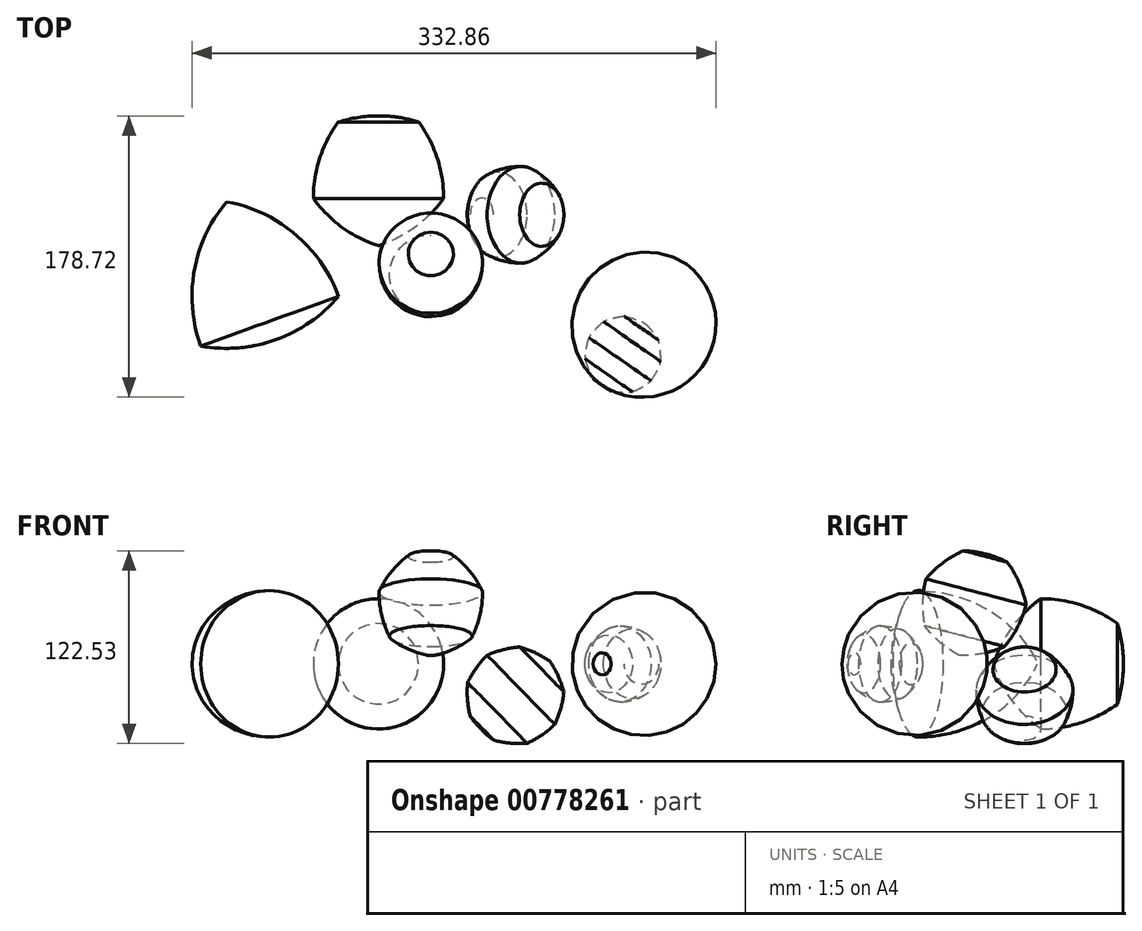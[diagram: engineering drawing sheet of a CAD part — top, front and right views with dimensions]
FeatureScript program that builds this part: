
annotation { "Feature Type Name" : "Feature", "Feature Type Description" : "" }
export const myFeature = defineFeature(function(context is Context, id is Id, definition is map)
    precondition{}
    {
        {
            var Q0;
            Q0=qCreatedBy(makeId("Top.planeOp"),FACE);
            var sketch = newSketch(context, id + "F0", { "sketchPlane" : qUnion([Q0])});
            skCircle(sketch, "E0.cCircle", {"center": v(-111.5, -42.3) * mm, "radius": 26.86 * mm, "construction": true});
            skLineSegment(sketch, "E0.0", {"start": v(-129.74, 8.22) * mm, "end": v(-58.63, -51.78) * mm});
            skLineSegment(sketch, "E0.1", {"start": v(-58.63, -51.78) * mm, "end": v(-146.14, -83.36) * mm});
            skLineSegment(sketch, "E0.2", {"start": v(-146.14, -83.36) * mm, "end": v(-129.74, 8.22) * mm});
            skPoint(sketch, "E0.0.midPoint", {"position": v(-94.18, -21.78) * mm});
            skCircle(sketch, "E1", {"center": v(-58.63, -51.78) * mm, "radius": 93.04 * mm});
            skCircle(sketch, "E2", {"center": v(-129.74, 8.22) * mm, "radius": 93.04 * mm});
            skCircle(sketch, "E3", {"center": v(-146.14, -83.36) * mm, "radius": 93.04 * mm});
            skLineSegment(sketch, "E4", {"start": v(-129.74, 8.22) * mm, "end": v(-98.18, -79.3) * mm});
            skSolve(sketch);
        }
        {
            var Q0;
            {var subQ0=sQuery(id+"F0.wireOp",EDGE,"E0.2");Q0=makeQuery(id+"F0.imprint","IMPRINT",FACE,{"disambiguationData":[TD([[makeQuery(id+"F0.imprint","IMPRINT",EDGE,{"derivedFrom":subQ0}),1.0]])]});}
            var Q1;
            {var subQ1=sQuery(id+"F0.wireOp",EDGE,"E0.2");Q1=makeQuery(id+"F0.imprint","IMPRINT",FACE,{"disambiguationData":[TD([[makeQuery(id+"F0.imprint","IMPRINT",EDGE,{"derivedFrom":subQ1}),-1.0]])]});}
            var Q2;
            {var subQ0=sQuery(id+"F0.wireOp",EDGE,"E2");var subQ3=sQuery(id+"F0.wireOp",EDGE,"E4");var subQ5=makeQuery(id+"F0.imprint","INTERSECT",VERTEX,{"derivedFrom":[subQ0,subQ3]});Q2=makeQuery(id+"F0.imprint","IMPRINT",FACE,{"disambiguationData":[TD([[makeQuery(id+"F0.imprint","IMPRINT",EDGE,{"disambiguationData":[TD([[subQ5,1.0]])],"derivedFrom":subQ3}),-1.0]])]});}
            var Q3;
            Q3=sQuery(id+"F0.wireOp",EDGE,"E4");
            revolve(context, id + "F1", {"surfaceOperationType" : NewSurfaceOperationType.NEW, "entities" : qUnion([Q0, Q1, Q2]), "axis" : qUnion([Q3]), "revolveType" : RevolveType.FULL});
        }
        {
            var Q0;
            Q0=qCreatedBy(makeId("Top.planeOp"),FACE);
            var sketch = newSketch(context, id + "F2", { "sketchPlane" : qUnion([Q0])});
            skCircle(sketch, "E5.cCircle", {"center": v(-33.28, 23.76) * mm, "radius": 35.16 * mm, "construction": true});
            skLineSegment(sketch, "E5.0", {"start": v(8.09, 10.45) * mm, "end": v(-33.16, -19.7) * mm});
            skLineSegment(sketch, "E5.1", {"start": v(-33.16, -19.7) * mm, "end": v(-74.57, 10.22) * mm});
            skLineSegment(sketch, "E5.2", {"start": v(-74.57, 10.22) * mm, "end": v(-58.92, 58.85) * mm});
            skLineSegment(sketch, "E5.3", {"start": v(-58.92, 58.85) * mm, "end": v(-7.83, 59) * mm});
            skLineSegment(sketch, "E5.4", {"start": v(-7.83, 59) * mm, "end": v(8.09, 10.45) * mm});
            skPoint(sketch, "E5.0.midPoint", {"position": v(-12.54, -4.62) * mm});
            skCircle(sketch, "E6", {"center": v(-7.83, 59) * mm, "radius": 82.66 * mm});
            skCircle(sketch, "E7", {"center": v(-58.92, 58.85) * mm, "radius": 82.66 * mm});
            skCircle(sketch, "E8", {"center": v(-74.57, 10.22) * mm, "radius": 82.66 * mm});
            skCircle(sketch, "E9", {"center": v(-33.16, -22.82) * mm, "radius": 85.64 * mm});
            skCircle(sketch, "E10", {"center": v(8.09, 10.45) * mm, "radius": 82.66 * mm});
            skLineSegment(sketch, "E11", {"start": v(-33.16, -22.82) * mm, "end": v(-33.28, 62.82) * mm});
            skSolve(sketch);
        }
        {
            var Q0;
            {var subQ1=sQuery(id+"F2.wireOp",EDGE,"E5.2");Q0=makeQuery(id+"F2.imprint","IMPRINT",FACE,{"disambiguationData":[TD([[makeQuery(id+"F2.imprint","IMPRINT",EDGE,{"derivedFrom":subQ1}),-1.0]])]});}
            var Q1;
            {var subQ0=sQuery(id+"F2.wireOp",EDGE,"E5.2");Q1=makeQuery(id+"F2.imprint","IMPRINT",FACE,{"disambiguationData":[TD([[makeQuery(id+"F2.imprint","IMPRINT",EDGE,{"derivedFrom":subQ0}),1.0]])]});}
            var Q2;
            {var subQ1=sQuery(id+"F2.wireOp",EDGE,"E5.1");var subQ3=sQuery(id+"F2.wireOp",EDGE,"E11");var subQ4=makeQuery(id+"F2.imprint","INTERSECT",VERTEX,{"derivedFrom":[subQ1,subQ3]});Q2=makeQuery(id+"F2.imprint","IMPRINT",FACE,{"disambiguationData":[TD([[makeQuery(id+"F2.imprint","IMPRINT",EDGE,{"disambiguationData":[TD([[subQ4,1.0]])],"derivedFrom":subQ3}),1.0]])]});}
            var Q3;
            {var subQ3=sQuery(id+"F2.wireOp",EDGE,"E11");var subQ5=sQuery(id+"F2.wireOp",EDGE,"E9");var subQ6=makeQuery(id+"F2.imprint","INTERSECT",VERTEX,{"derivedFrom":[subQ5,subQ3]});Q3=makeQuery(id+"F2.imprint","IMPRINT",FACE,{"disambiguationData":[TD([[makeQuery(id+"F2.imprint","IMPRINT",EDGE,{"disambiguationData":[TD([[subQ6,-1.0]])],"derivedFrom":subQ5}),1.0]])]});}
            var Q4;
            Q4=sQuery(id+"F2.wireOp",EDGE,"E11");
            revolve(context, id + "F3", {"surfaceOperationType" : NewSurfaceOperationType.NEW, "entities" : qUnion([Q0, Q1, Q2, Q3]), "axis" : qUnion([Q4]), "revolveType" : RevolveType.FULL});
        }
        {
            var Q0;
            Q0=qCreatedBy(makeId("Right.planeOp"),FACE);
            var sketch = newSketch(context, id + "F4", { "sketchPlane" : qUnion([Q0])});
            skCircle(sketch, "E12.cCircle", {"center": v(-33.27, 38.47) * mm, "radius": 30.9 * mm, "construction": true});
            skLineSegment(sketch, "E12.0", {"start": v(1.02, 37.4) * mm, "end": v(-12.72, 11) * mm});
            skLineSegment(sketch, "E12.1", {"start": v(-12.72, 11) * mm, "end": v(-41.93, 5.28) * mm});
            skLineSegment(sketch, "E12.2", {"start": v(-41.93, 5.28) * mm, "end": v(-64.62, 24.55) * mm});
            skLineSegment(sketch, "E12.3", {"start": v(-64.62, 24.55) * mm, "end": v(-63.7, 54.3) * mm});
            skLineSegment(sketch, "E12.4", {"start": v(-63.7, 54.3) * mm, "end": v(-39.86, 72.13) * mm});
            skLineSegment(sketch, "E12.5", {"start": v(-39.86, 72.13) * mm, "end": v(-11.06, 64.6) * mm});
            skLineSegment(sketch, "E12.6", {"start": v(-11.06, 64.6) * mm, "end": v(1.02, 37.4) * mm});
            skPoint(sketch, "E12.0.midPoint", {"position": v(-5.85, 24.2) * mm});
            skCircle(sketch, "E13", {"center": v(-39.86, 72.13) * mm, "radius": 66.89 * mm});
            skCircle(sketch, "E14", {"center": v(-63.7, 54.3) * mm, "radius": 66.89 * mm});
            skCircle(sketch, "E15", {"center": v(-64.62, 24.55) * mm, "radius": 66.89 * mm});
            skCircle(sketch, "E16", {"center": v(-41.38, 5.18) * mm, "radius": 66.72 * mm});
            skCircle(sketch, "E17", {"center": v(-12.72, 11) * mm, "radius": 66.89 * mm});
            skCircle(sketch, "E18", {"center": v(1.02, 37.4) * mm, "radius": 66.89 * mm});
            skLineSegment(sketch, "E19", {"start": v(-41.38, 5.18) * mm, "end": v(-24.52, 69.73) * mm});
            skSolve(sketch);
        }
        {
            var Q0;
            {var subQ5=sQuery(id+"F4.wireOp",EDGE,"E12.0");Q0=makeQuery(id+"F4.imprint","IMPRINT",FACE,{"disambiguationData":[TD([[makeQuery(id+"F4.imprint","IMPRINT",EDGE,{"derivedFrom":subQ5}),-1.0]])]});}
            var Q1;
            {var subQ0=sQuery(id+"F4.wireOp",EDGE,"E16");var subQ3=sQuery(id+"F4.wireOp",EDGE,"E19");var subQ5=makeQuery(id+"F4.imprint","INTERSECT",VERTEX,{"derivedFrom":[subQ0,subQ3]});Q1=makeQuery(id+"F4.imprint","IMPRINT",FACE,{"disambiguationData":[TD([[makeQuery(id+"F4.imprint","IMPRINT",EDGE,{"disambiguationData":[TD([[subQ5,1.0]])],"derivedFrom":subQ3}),-1.0]])]});}
            var Q2;
            {var subQ0=sQuery(id+"F4.wireOp",EDGE,"E12.6");Q2=makeQuery(id+"F4.imprint","IMPRINT",FACE,{"disambiguationData":[TD([[makeQuery(id+"F4.imprint","IMPRINT",EDGE,{"derivedFrom":subQ0}),1.0]])]});}
            var Q3;
            {var subQ0=sQuery(id+"F4.wireOp",EDGE,"E13");var subQ3=sQuery(id+"F4.wireOp",EDGE,"E19");var subQ5=makeQuery(id+"F4.imprint","INTERSECT",VERTEX,{"derivedFrom":[subQ0,subQ3]});Q3=makeQuery(id+"F4.imprint","IMPRINT",FACE,{"disambiguationData":[TD([[makeQuery(id+"F4.imprint","IMPRINT",EDGE,{"disambiguationData":[TD([[subQ5,-1.0]])],"derivedFrom":subQ3}),-1.0]])]});}
            var Q4;
            {var subQ0=sQuery(id+"F4.wireOp",EDGE,"E12.0");Q4=makeQuery(id+"F4.imprint","IMPRINT",FACE,{"disambiguationData":[TD([[makeQuery(id+"F4.imprint","IMPRINT",EDGE,{"derivedFrom":subQ0}),1.0]])]});}
            var Q5;
            Q5=sQuery(id+"F4.wireOp",EDGE,"E19");
            revolve(context, id + "F5", {"surfaceOperationType" : NewSurfaceOperationType.NEW, "entities" : qUnion([Q0, Q1, Q2, Q3, Q4]), "axis" : qUnion([Q5]), "revolveType" : RevolveType.FULL});
        }
        {
            var Q0;
            Q0=qCreatedBy(makeId("Front.planeOp"),FACE);
            var sketch = newSketch(context, id + "F6", { "sketchPlane" : qUnion([Q0])});
            skCircle(sketch, "E20.cCircle", {"center": v(53.42, -20.3) * mm, "radius": 29.3 * mm, "construction": true});
            skLineSegment(sketch, "E20.0", {"start": v(23.4, -11.91) * mm, "end": v(35.8, 5.43) * mm});
            skLineSegment(sketch, "E20.1", {"start": v(35.8, 5.43) * mm, "end": v(56.46, 10.73) * mm});
            skLineSegment(sketch, "E20.2", {"start": v(56.46, 10.73) * mm, "end": v(75.7, 1.51) * mm});
            skLineSegment(sketch, "E20.3", {"start": v(75.7, 1.51) * mm, "end": v(84.5, -17.9) * mm});
            skLineSegment(sketch, "E20.4", {"start": v(84.5, -17.9) * mm, "end": v(78.77, -38.45) * mm});
            skLineSegment(sketch, "E20.5", {"start": v(78.77, -38.45) * mm, "end": v(61.17, -50.5) * mm});
            skLineSegment(sketch, "E20.6", {"start": v(61.17, -50.5) * mm, "end": v(39.95, -48.41) * mm});
            skLineSegment(sketch, "E20.7", {"start": v(39.95, -48.41) * mm, "end": v(25.03, -33.18) * mm});
            skLineSegment(sketch, "E20.8", {"start": v(25.03, -33.18) * mm, "end": v(23.4, -11.91) * mm});
            skPoint(sketch, "E20.0.midPoint", {"position": v(29.6, -3.24) * mm});
            skCircle(sketch, "E21", {"center": v(35.8, 5.43) * mm, "radius": 61.4 * mm});
            skCircle(sketch, "E22", {"center": v(56.46, 10.73) * mm, "radius": 61.4 * mm});
            skCircle(sketch, "E23", {"center": v(75.7, 1.51) * mm, "radius": 61.4 * mm});
            skCircle(sketch, "E24", {"center": v(84.5, -17.9) * mm, "radius": 61.4 * mm});
            skCircle(sketch, "E25", {"center": v(78.77, -38.45) * mm, "radius": 61.4 * mm});
            skCircle(sketch, "E26", {"center": v(61.17, -50.5) * mm, "radius": 61.4 * mm});
            skCircle(sketch, "E27", {"center": v(39.95, -48.41) * mm, "radius": 61.4 * mm});
            skCircle(sketch, "E28", {"center": v(25.03, -33.18) * mm, "radius": 61.4 * mm});
            skCircle(sketch, "E29", {"center": v(23.4, -11.91) * mm, "radius": 61.4 * mm});
            skLineSegment(sketch, "E30", {"start": v(75.7, 1.51) * mm, "end": v(32.49, -40.8) * mm});
            skLineSegment(sketch, "E31", {"start": v(32.49, -40.8) * mm, "end": v(31.82, -41.45) * mm});
            skSolve(sketch);
        }
        {
            var Q0;
            Q0=makeQuery(id+"F6.imprint","IMPRINT",FACE,{"disambiguationData":[TD([[makeQuery(id+"F6.imprint","IMPRINT",EDGE,{"derivedFrom":sQuery(id+"F6.wireOp",EDGE,"E20.0")}),-1.0]])]});
            var Q1;
            {var subQ0=sQuery(id+"F6.wireOp",EDGE,"E20.2");Q1=makeQuery(id+"F6.imprint","IMPRINT",FACE,{"disambiguationData":[TD([[makeQuery(id+"F6.imprint","IMPRINT",EDGE,{"derivedFrom":subQ0}),1.0]])]});}
            var Q2;
            {var subQ0=sQuery(id+"F6.wireOp",EDGE,"E20.1");Q2=makeQuery(id+"F6.imprint","IMPRINT",FACE,{"disambiguationData":[TD([[makeQuery(id+"F6.imprint","IMPRINT",EDGE,{"derivedFrom":subQ0}),1.0]])]});}
            var Q3;
            {var subQ0=sQuery(id+"F6.wireOp",EDGE,"E20.0");Q3=makeQuery(id+"F6.imprint","IMPRINT",FACE,{"disambiguationData":[TD([[makeQuery(id+"F6.imprint","IMPRINT",EDGE,{"derivedFrom":subQ0}),1.0]])]});}
            var Q4;
            {var subQ0=sQuery(id+"F6.wireOp",EDGE,"E20.8");Q4=makeQuery(id+"F6.imprint","IMPRINT",FACE,{"disambiguationData":[TD([[makeQuery(id+"F6.imprint","IMPRINT",EDGE,{"derivedFrom":subQ0}),1.0]])]});}
            var Q5;
            {var subQ3=sQuery(id+"F6.wireOp",EDGE,"E31");Q5=makeQuery(id+"F6.imprint","IMPRINT",FACE,{"disambiguationData":[TD([[makeQuery(id+"F6.imprint","IMPRINT",EDGE,{"derivedFrom":subQ3}),-1.0]])]});}
            var Q6;
            Q6=sQuery(id+"F6.wireOp",EDGE,"E30");
            revolve(context, id + "F7", {"surfaceOperationType" : NewSurfaceOperationType.NEW, "entities" : qUnion([Q0, Q1, Q2, Q3, Q4, Q5]), "axis" : qUnion([Q6]), "revolveType" : RevolveType.FULL});
        }
        {
            var Q0;
            Q0=qCreatedBy(makeId("Top.planeOp"),FACE);
            var sketch = newSketch(context, id + "F8", { "sketchPlane" : qUnion([Q0])});
            skCircle(sketch, "E32.cCircle", {"center": v(122.11, -88.9) * mm, "radius": 23.35 * mm, "construction": true});
            skLineSegment(sketch, "E32.0", {"start": v(97.9, -91.44) * mm, "end": v(100.37, -77.95) * mm});
            skLineSegment(sketch, "E32.1", {"start": v(100.37, -77.95) * mm, "end": v(109.74, -67.94) * mm});
            skLineSegment(sketch, "E32.2", {"start": v(109.74, -67.94) * mm, "end": v(123.04, -64.58) * mm});
            skLineSegment(sketch, "E32.3", {"start": v(123.04, -64.58) * mm, "end": v(136.04, -68.94) * mm});
            skLineSegment(sketch, "E32.4", {"start": v(136.04, -68.94) * mm, "end": v(144.62, -79.63) * mm});
            skLineSegment(sketch, "E32.5", {"start": v(144.62, -79.63) * mm, "end": v(146.05, -93.27) * mm});
            skLineSegment(sketch, "E32.6", {"start": v(146.05, -93.27) * mm, "end": v(139.89, -105.52) * mm});
            skLineSegment(sketch, "E32.7", {"start": v(139.89, -105.52) * mm, "end": v(128.08, -112.5) * mm});
            skLineSegment(sketch, "E32.8", {"start": v(128.08, -112.5) * mm, "end": v(114.38, -111.97) * mm});
            skLineSegment(sketch, "E32.9", {"start": v(114.38, -111.97) * mm, "end": v(103.13, -104.12) * mm});
            skLineSegment(sketch, "E32.10", {"start": v(103.13, -104.12) * mm, "end": v(97.9, -91.44) * mm});
            skPoint(sketch, "E32.0.midPoint", {"position": v(99.14, -84.7) * mm});
            skCircle(sketch, "E33", {"center": v(97.9, -91.44) * mm, "radius": 48.18 * mm});
            skCircle(sketch, "E34", {"center": v(100.37, -77.95) * mm, "radius": 48.18 * mm});
            skCircle(sketch, "E35", {"center": v(109.74, -67.94) * mm, "radius": 48.18 * mm});
            skCircle(sketch, "E36", {"center": v(123.04, -64.58) * mm, "radius": 48.18 * mm});
            skCircle(sketch, "E37", {"center": v(134.23, -68.94) * mm, "radius": 46.96 * mm});
            skCircle(sketch, "E38", {"center": v(144.91, -79.68) * mm, "radius": 48.45 * mm});
            skCircle(sketch, "E39", {"center": v(146.05, -93.27) * mm, "radius": 48.18 * mm});
            skCircle(sketch, "E40", {"center": v(139.89, -105.52) * mm, "radius": 48.18 * mm});
            skCircle(sketch, "E41", {"center": v(128.08, -112.5) * mm, "radius": 48.18 * mm});
            skCircle(sketch, "E42", {"center": v(114.38, -111.97) * mm, "radius": 48.18 * mm});
            skCircle(sketch, "E43", {"center": v(103.13, -104.12) * mm, "radius": 48.18 * mm});
            skLineSegment(sketch, "E44", {"start": v(136.04, -68.94) * mm, "end": v(108.59, -108.28) * mm});
            skSolve(sketch);
        }
        {
            var Q0;
            Q0=makeQuery(id+"F8.imprint","IMPRINT",FACE,{"disambiguationData":[TD([[makeQuery(id+"F8.imprint","IMPRINT",EDGE,{"derivedFrom":sQuery(id+"F8.wireOp",EDGE,"E32.0")}),-1.0]])]});
            var Q1;
            {var subQ0=sQuery(id+"F8.wireOp",EDGE,"E37");var subQ3=sQuery(id+"F8.wireOp",EDGE,"E44");var subQ5=makeQuery(id+"F8.imprint","INTERSECT",VERTEX,{"derivedFrom":[subQ0,subQ3]});Q1=makeQuery(id+"F8.imprint","IMPRINT",FACE,{"disambiguationData":[TD([[makeQuery(id+"F8.imprint","IMPRINT",EDGE,{"disambiguationData":[TD([[subQ5,1.0]])],"derivedFrom":subQ3}),-1.0]])]});}
            var Q2;
            {var subQ0=sQuery(id+"F8.wireOp",EDGE,"E32.10");Q2=makeQuery(id+"F8.imprint","IMPRINT",FACE,{"disambiguationData":[TD([[makeQuery(id+"F8.imprint","IMPRINT",EDGE,{"derivedFrom":subQ0}),1.0]])]});}
            var Q3;
            {var subQ0=sQuery(id+"F8.wireOp",EDGE,"E32.0");Q3=makeQuery(id+"F8.imprint","IMPRINT",FACE,{"disambiguationData":[TD([[makeQuery(id+"F8.imprint","IMPRINT",EDGE,{"derivedFrom":subQ0}),1.0]])]});}
            var Q4;
            {var subQ0=sQuery(id+"F8.wireOp",EDGE,"E32.1");Q4=makeQuery(id+"F8.imprint","IMPRINT",FACE,{"disambiguationData":[TD([[makeQuery(id+"F8.imprint","IMPRINT",EDGE,{"derivedFrom":subQ0}),1.0]])]});}
            var Q5;
            {var subQ0=sQuery(id+"F8.wireOp",EDGE,"E32.2");Q5=makeQuery(id+"F8.imprint","IMPRINT",FACE,{"disambiguationData":[TD([[makeQuery(id+"F8.imprint","IMPRINT",EDGE,{"derivedFrom":subQ0}),1.0]])]});}
            var Q6;
            {var subQ0=sQuery(id+"F8.wireOp",EDGE,"E32.3");Q6=makeQuery(id+"F8.imprint","IMPRINT",FACE,{"disambiguationData":[TD([[makeQuery(id+"F8.imprint","IMPRINT",EDGE,{"derivedFrom":subQ0}),1.0]])]});}
            var Q7;
            Q7=sQuery(id+"F8.wireOp",EDGE,"E44");
            revolve(context, id + "F9", {"surfaceOperationType" : NewSurfaceOperationType.NEW, "entities" : qUnion([Q0, Q1, Q2, Q3, Q4, Q5, Q6]), "axis" : qUnion([Q7]), "revolveType" : RevolveType.FULL});
        }
    });
